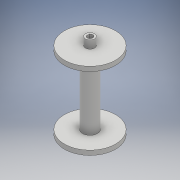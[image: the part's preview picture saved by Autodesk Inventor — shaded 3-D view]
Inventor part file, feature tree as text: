
AUTODESK INVENTOR PART (.ipt)
format: ipt  version: 2017 (Build 210142000, 142)  size: 167,936 bytes
history: native  units: mm
features: sketch x3, extrude x2, revolve x1
ambient origin geometry x8: Origin, YZ Plane, XZ Plane, XY Plane, X Axis, Y Axis, Z Axis, Center Point
bodies: Body1 (feature_tree)
feature tree (6):
  revolve  "Revolution2"  [1 undecoded]
  extrude  "Extrusion6"  Depth=7.0mm
  extrude  "Extrusion7"  Depth=4.0mm
  sketch  "Sketch1"  dims[d1=2.5mm d2=4.0mm]
  sketch  "Sketch6"  dims[d3=7.0mm d4=20.0mm]
  sketch  "Sketch7"  dims[d5=34.0mm d9=4.0mm d12=2.5mm d13=4.0mm d55=22.5mm d56=4.0mm d57=90.0deg d64=20.0mm d65=90.0deg d69=15.0mm d71=15.0mm d73=5.0mm d74=0.0mm d75=2.5mm d76=5.0mm d77=5.0mm d78=26.0mm d79=0.0mm]
note: 1 required parameter value undecoded (feature->parameter linkage not recoverable at this tier; creation-order binding heuristic only, values carry confidence <= 0.55)
